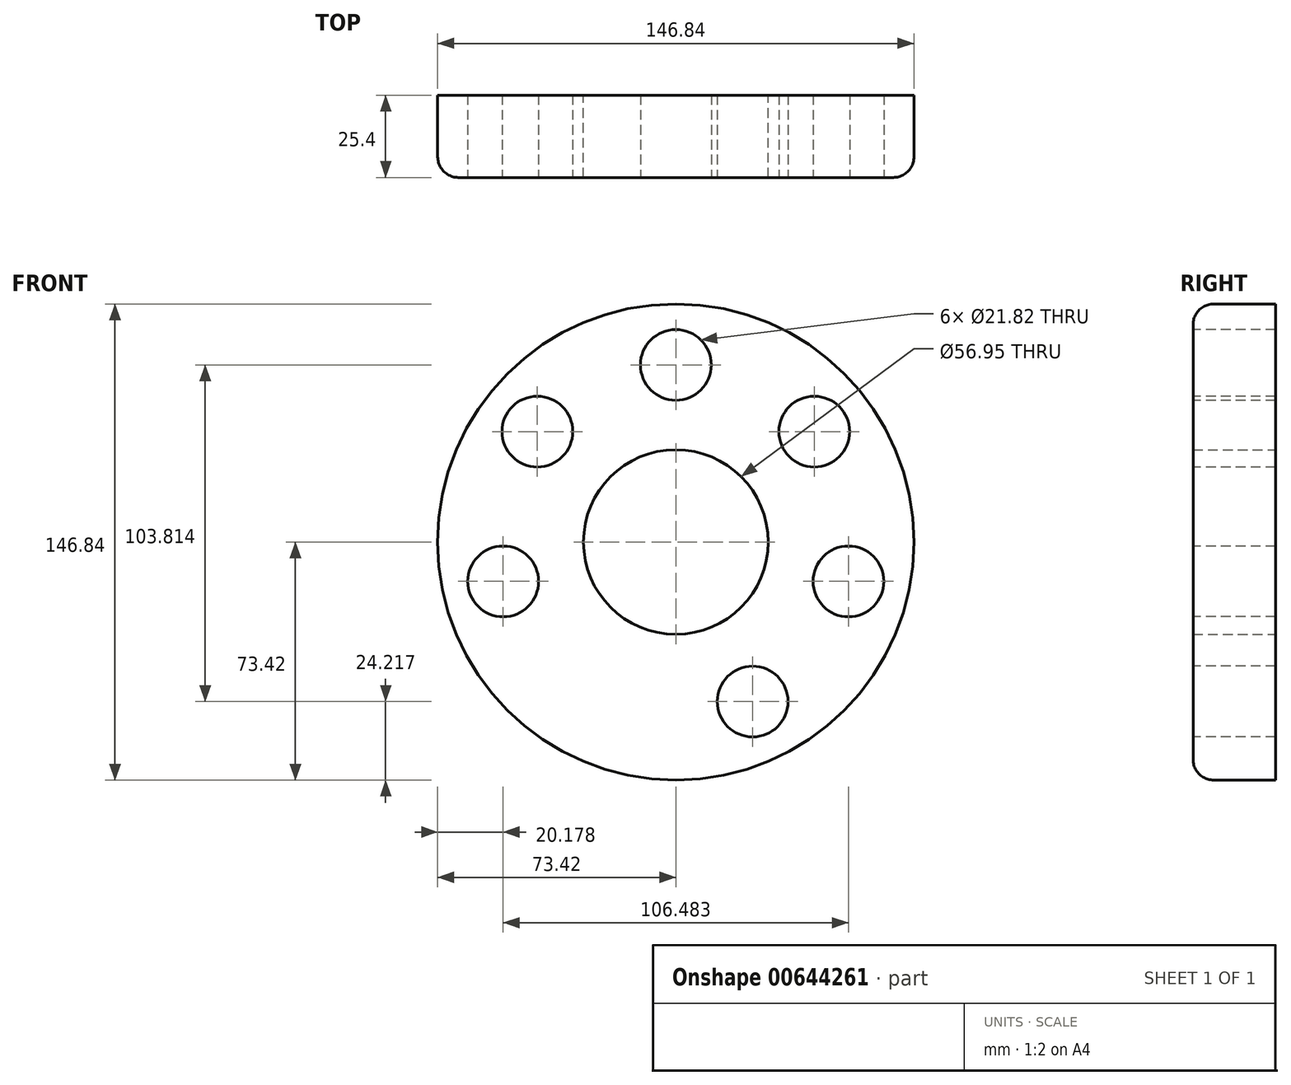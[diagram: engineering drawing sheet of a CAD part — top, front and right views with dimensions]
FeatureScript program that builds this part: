
annotation { "Feature Type Name" : "Feature", "Feature Type Description" : "" }
export const myFeature = defineFeature(function(context is Context, id is Id, definition is map)
    precondition{}
    {
        {
            var Q0;
            Q0=qCreatedBy(makeId("Front.planeOp"),FACE);
            var sketch = newSketch(context, id + "F0", { "sketchPlane" : qUnion([Q0])});
            skCircle(sketch, "E0", {"center": v(0, 0) * mm, "radius": 73.42 * mm});
            skSolve(sketch);
        }
        {
            var Q0;
            Q0=makeQuery(id+"F0.imprint","IMPRINT",FACE,{"disambiguationData":[TD([[makeQuery(id+"F0.imprint","IMPRINT",EDGE,{"derivedFrom":sQuery(id+"F0.wireOp",EDGE,"E0")}),1.0]])]});
            extrude(context, id + "F1", {"entities" : qUnion([Q0]), "depth" : 25.4 * mm, "offsetDistance" : 25.4 * mm});
        }
        {
            var Q0;
            Q0=makeQuery(id+"F1.opExtrude","CAP_FACE",FACE,{"disambiguationData":[OSD([sQuery(id+"F0.wireOp",EDGE,"E0")])],"isStart":false});
            var sketch = newSketch(context, id + "F2", { "sketchPlane" : qUnion([Q0])});
            skCircle(sketch, "E1.0", {"center": v(0, 0) * mm, "radius": 54.37 * mm});
            skSolve(sketch);
        }
        {
            var Q0;
            Q0=makeQuery(id+"F1.opExtrude","CAP_EDGE",EDGE,{"disambiguationData":[OSD([sQuery(id+"F0.wireOp",EDGE,"E0")])],"isStart":false});
            fillet(context, id + "F3", {"entities" : qUnion([Q0]), "radius" : 6.35 * mm, "tangentPropagation" : true, "allowEdgeOverflow" : false});
        }
        {
            var Q0;
            Q0=makeQuery(id+"F2.imprint","IMPRINT",FACE,{"disambiguationData":[TD([[makeQuery(id+"F2.imprint","IMPRINT",EDGE,{"derivedFrom":sQuery(id+"F2.wireOp",EDGE,"E1.0")}),1.0]])]});
            var sketch = newSketch(context, id + "F4", { "sketchPlane" : qUnion([Q0])});
            skCircle(sketch, "E2", {"center": v(0, 54.61) * mm, "radius": 10.9 * mm});
            skCircle(sketch, "E3.1.0", {"center": v(-42.7, 34.05) * mm, "radius": 10.9 * mm});
            skCircle(sketch, "E3.2.0", {"center": v(-53.24, -12.15) * mm, "radius": 10.9 * mm});
            skCircle(sketch, "E3.3.0", {"center": v(-23.7, -49.2) * mm, "radius": 10.9 * mm});
            skCircle(sketch, "E3.4.0", {"center": v(23.7, -49.2) * mm, "radius": 10.9 * mm});
            skCircle(sketch, "E3.5.0", {"center": v(53.24, -12.15) * mm, "radius": 10.9 * mm});
            skCircle(sketch, "E3.6.0", {"center": v(42.7, 34.05) * mm, "radius": 10.9 * mm});
            skPoint(sketch, "E3.center", {"position": v(0, 0) * mm});
            skSolve(sketch);
        }
        {
            var Q0;
            {var subQ0=sQuery(id+"F4.wireOp",EDGE,"E2");var subQ1=makeQuery(id+"F2.imprint","IMPRINT",EDGE,{"derivedFrom":sQuery(id+"F2.wireOp",EDGE,"E1.0")});var subQ2=makeQuery(id+"F4.imprint","INTERSECT",VERTEX,{"disambiguationData":[OD(0.0)],"derivedFrom":[subQ1,subQ0]});Q0=makeQuery(id+"F4.imprint","IMPRINT",FACE,{"disambiguationData":[TD([[makeQuery(id+"F4.imprint","IMPRINT",EDGE,{"disambiguationData":[TD([[subQ2,1.0]])],"derivedFrom":subQ0}),1.0]])]});}
            var Q1;
            {var subQ0=sQuery(id+"F4.wireOp",EDGE,"E2");var subQ1=makeQuery(id+"F2.imprint","IMPRINT",EDGE,{"derivedFrom":sQuery(id+"F2.wireOp",EDGE,"E1.0")});var subQ2=makeQuery(id+"F4.imprint","INTERSECT",VERTEX,{"disambiguationData":[OD(0.0)],"derivedFrom":[subQ1,subQ0]});Q1=makeQuery(id+"F4.imprint","IMPRINT",FACE,{"disambiguationData":[TD([[makeQuery(id+"F4.imprint","IMPRINT",EDGE,{"disambiguationData":[TD([[subQ2,-1.0]])],"derivedFrom":subQ0}),1.0]])]});}
            var Q2;
            {var subQ0=sQuery(id+"F4.wireOp",EDGE,"E3.6.0");var subQ1=makeQuery(id+"F2.imprint","IMPRINT",EDGE,{"derivedFrom":sQuery(id+"F2.wireOp",EDGE,"E1.0")});var subQ2=makeQuery(id+"F4.imprint","INTERSECT",VERTEX,{"disambiguationData":[OD(0.0)],"derivedFrom":[subQ1,subQ0]});Q2=makeQuery(id+"F4.imprint","IMPRINT",FACE,{"disambiguationData":[TD([[makeQuery(id+"F4.imprint","IMPRINT",EDGE,{"disambiguationData":[TD([[subQ2,1.0]])],"derivedFrom":subQ0}),1.0]])]});}
            var Q3;
            {var subQ0=sQuery(id+"F4.wireOp",EDGE,"E3.6.0");var subQ1=makeQuery(id+"F2.imprint","IMPRINT",EDGE,{"derivedFrom":sQuery(id+"F2.wireOp",EDGE,"E1.0")});var subQ2=makeQuery(id+"F4.imprint","INTERSECT",VERTEX,{"disambiguationData":[OD(0.0)],"derivedFrom":[subQ1,subQ0]});Q3=makeQuery(id+"F4.imprint","IMPRINT",FACE,{"disambiguationData":[TD([[makeQuery(id+"F4.imprint","IMPRINT",EDGE,{"disambiguationData":[TD([[subQ2,-1.0]])],"derivedFrom":subQ0}),1.0]])]});}
            var Q4;
            {var subQ0=sQuery(id+"F4.wireOp",EDGE,"E3.5.0");var subQ1=makeQuery(id+"F2.imprint","IMPRINT",EDGE,{"derivedFrom":sQuery(id+"F2.wireOp",EDGE,"E1.0")});var subQ2=makeQuery(id+"F4.imprint","INTERSECT",VERTEX,{"disambiguationData":[OD(0.0)],"derivedFrom":[subQ1,subQ0]});Q4=makeQuery(id+"F4.imprint","IMPRINT",FACE,{"disambiguationData":[TD([[makeQuery(id+"F4.imprint","IMPRINT",EDGE,{"disambiguationData":[TD([[subQ2,-1.0]])],"derivedFrom":subQ0}),1.0]])]});}
            var Q5;
            {var subQ0=sQuery(id+"F4.wireOp",EDGE,"E3.5.0");var subQ1=makeQuery(id+"F2.imprint","IMPRINT",EDGE,{"derivedFrom":sQuery(id+"F2.wireOp",EDGE,"E1.0")});var subQ2=makeQuery(id+"F4.imprint","INTERSECT",VERTEX,{"disambiguationData":[OD(0.0)],"derivedFrom":[subQ1,subQ0]});Q5=makeQuery(id+"F4.imprint","IMPRINT",FACE,{"disambiguationData":[TD([[makeQuery(id+"F4.imprint","IMPRINT",EDGE,{"disambiguationData":[TD([[subQ2,1.0]])],"derivedFrom":subQ0}),1.0]])]});}
            var Q6;
            {var subQ0=sQuery(id+"F4.wireOp",EDGE,"E3.4.0");var subQ1=makeQuery(id+"F2.imprint","IMPRINT",EDGE,{"derivedFrom":sQuery(id+"F2.wireOp",EDGE,"E1.0")});var subQ2=makeQuery(id+"F4.imprint","INTERSECT",VERTEX,{"disambiguationData":[OD(0.0)],"derivedFrom":[subQ1,subQ0]});Q6=makeQuery(id+"F4.imprint","IMPRINT",FACE,{"disambiguationData":[TD([[makeQuery(id+"F4.imprint","IMPRINT",EDGE,{"disambiguationData":[TD([[subQ2,1.0]])],"derivedFrom":subQ0}),1.0]])]});}
            var Q7;
            {var subQ0=sQuery(id+"F4.wireOp",EDGE,"E3.4.0");var subQ1=makeQuery(id+"F2.imprint","IMPRINT",EDGE,{"derivedFrom":sQuery(id+"F2.wireOp",EDGE,"E1.0")});var subQ2=makeQuery(id+"F4.imprint","INTERSECT",VERTEX,{"disambiguationData":[OD(0.0)],"derivedFrom":[subQ1,subQ0]});Q7=makeQuery(id+"F4.imprint","IMPRINT",FACE,{"disambiguationData":[TD([[makeQuery(id+"F4.imprint","IMPRINT",EDGE,{"disambiguationData":[TD([[subQ2,-1.0]])],"derivedFrom":subQ0}),1.0]])]});}
            var Q8;
            {var subQ1=makeQuery(id+"F2.imprint","IMPRINT",EDGE,{"derivedFrom":sQuery(id+"F2.wireOp",EDGE,"E1.0")});var subQ4=makeQuery(id+"F4.imprint","IMPRINT",VERTEX,{"derivedFrom":subQ1});Q8=makeQuery(id+"F4.imprint","IMPRINT",FACE,{"disambiguationData":[TD([[makeQuery(id+"F4.imprint","IMPRINT",EDGE,{"disambiguationData":[TD([[subQ4,1.0]])],"derivedFrom":subQ1}),1.0]])]});}
            var Q9;
            {var subQ1=makeQuery(id+"F2.imprint","IMPRINT",EDGE,{"derivedFrom":sQuery(id+"F2.wireOp",EDGE,"E1.0")});var subQ4=makeQuery(id+"F4.imprint","IMPRINT",VERTEX,{"derivedFrom":subQ1});Q9=makeQuery(id+"F4.imprint","IMPRINT",FACE,{"disambiguationData":[TD([[makeQuery(id+"F4.imprint","IMPRINT",EDGE,{"disambiguationData":[TD([[subQ4,1.0]])],"derivedFrom":subQ1}),-1.0]])]});}
            var Q10;
            {var subQ0=sQuery(id+"F4.wireOp",EDGE,"E3.2.0");var subQ1=makeQuery(id+"F2.imprint","IMPRINT",EDGE,{"derivedFrom":sQuery(id+"F2.wireOp",EDGE,"E1.0")});var subQ2=makeQuery(id+"F4.imprint","INTERSECT",VERTEX,{"disambiguationData":[OD(0.0)],"derivedFrom":[subQ1,subQ0]});Q10=makeQuery(id+"F4.imprint","IMPRINT",FACE,{"disambiguationData":[TD([[makeQuery(id+"F4.imprint","IMPRINT",EDGE,{"disambiguationData":[TD([[subQ2,-1.0]])],"derivedFrom":subQ0}),1.0]])]});}
            var Q11;
            {var subQ0=sQuery(id+"F4.wireOp",EDGE,"E3.2.0");var subQ1=makeQuery(id+"F2.imprint","IMPRINT",EDGE,{"derivedFrom":sQuery(id+"F2.wireOp",EDGE,"E1.0")});var subQ2=makeQuery(id+"F4.imprint","INTERSECT",VERTEX,{"disambiguationData":[OD(0.0)],"derivedFrom":[subQ1,subQ0]});Q11=makeQuery(id+"F4.imprint","IMPRINT",FACE,{"disambiguationData":[TD([[makeQuery(id+"F4.imprint","IMPRINT",EDGE,{"disambiguationData":[TD([[subQ2,1.0]])],"derivedFrom":subQ0}),1.0]])]});}
            var Q12;
            {var subQ0=sQuery(id+"F4.wireOp",EDGE,"E3.1.0");var subQ1=makeQuery(id+"F2.imprint","IMPRINT",EDGE,{"derivedFrom":sQuery(id+"F2.wireOp",EDGE,"E1.0")});var subQ2=makeQuery(id+"F4.imprint","INTERSECT",VERTEX,{"disambiguationData":[OD(0.0)],"derivedFrom":[subQ1,subQ0]});Q12=makeQuery(id+"F4.imprint","IMPRINT",FACE,{"disambiguationData":[TD([[makeQuery(id+"F4.imprint","IMPRINT",EDGE,{"disambiguationData":[TD([[subQ2,1.0]])],"derivedFrom":subQ0}),1.0]])]});}
            var Q13;
            {var subQ0=sQuery(id+"F4.wireOp",EDGE,"E3.1.0");var subQ1=makeQuery(id+"F2.imprint","IMPRINT",EDGE,{"derivedFrom":sQuery(id+"F2.wireOp",EDGE,"E1.0")});var subQ2=makeQuery(id+"F4.imprint","INTERSECT",VERTEX,{"disambiguationData":[OD(0.0)],"derivedFrom":[subQ1,subQ0]});Q13=makeQuery(id+"F4.imprint","IMPRINT",FACE,{"disambiguationData":[TD([[makeQuery(id+"F4.imprint","IMPRINT",EDGE,{"disambiguationData":[TD([[subQ2,-1.0]])],"derivedFrom":subQ0}),1.0]])]});}
            extrude(context, id + "F5", {"entities" : qUnion([Q0, Q1, Q2, Q3, Q4, Q5, Q6, Q7, Q8, Q9, Q10, Q11, Q12, Q13]), "operationType" : NewBodyOperationType.REMOVE, "oppositeDirection" : true, "depth" : 25.4 * mm, "offsetDistance" : 25.4 * mm});
        }
        {
            var Q0;
            Q0=makeQuery(id+"F1.opExtrude","CAP_FACE",FACE,{"disambiguationData":[OSD([sQuery(id+"F0.wireOp",EDGE,"E0")])],"isStart":true});
            var sketch = newSketch(context, id + "F6", { "sketchPlane" : qUnion([Q0])});
            skCircle(sketch, "E4", {"center": v(0, 0) * mm, "radius": 28.47 * mm});
            skSolve(sketch);
        }
        {
            var Q0;
            Q0=makeQuery(id+"F6.imprint","IMPRINT",FACE,{"disambiguationData":[TD([[makeQuery(id+"F6.imprint","IMPRINT",EDGE,{"derivedFrom":sQuery(id+"F6.wireOp",EDGE,"E4")}),1.0]])]});
            extrude(context, id + "F7", {"entities" : qUnion([Q0]), "operationType" : NewBodyOperationType.REMOVE, "oppositeDirection" : true, "depth" : 25.4 * mm, "offsetDistance" : 25.4 * mm});
        }
    });
